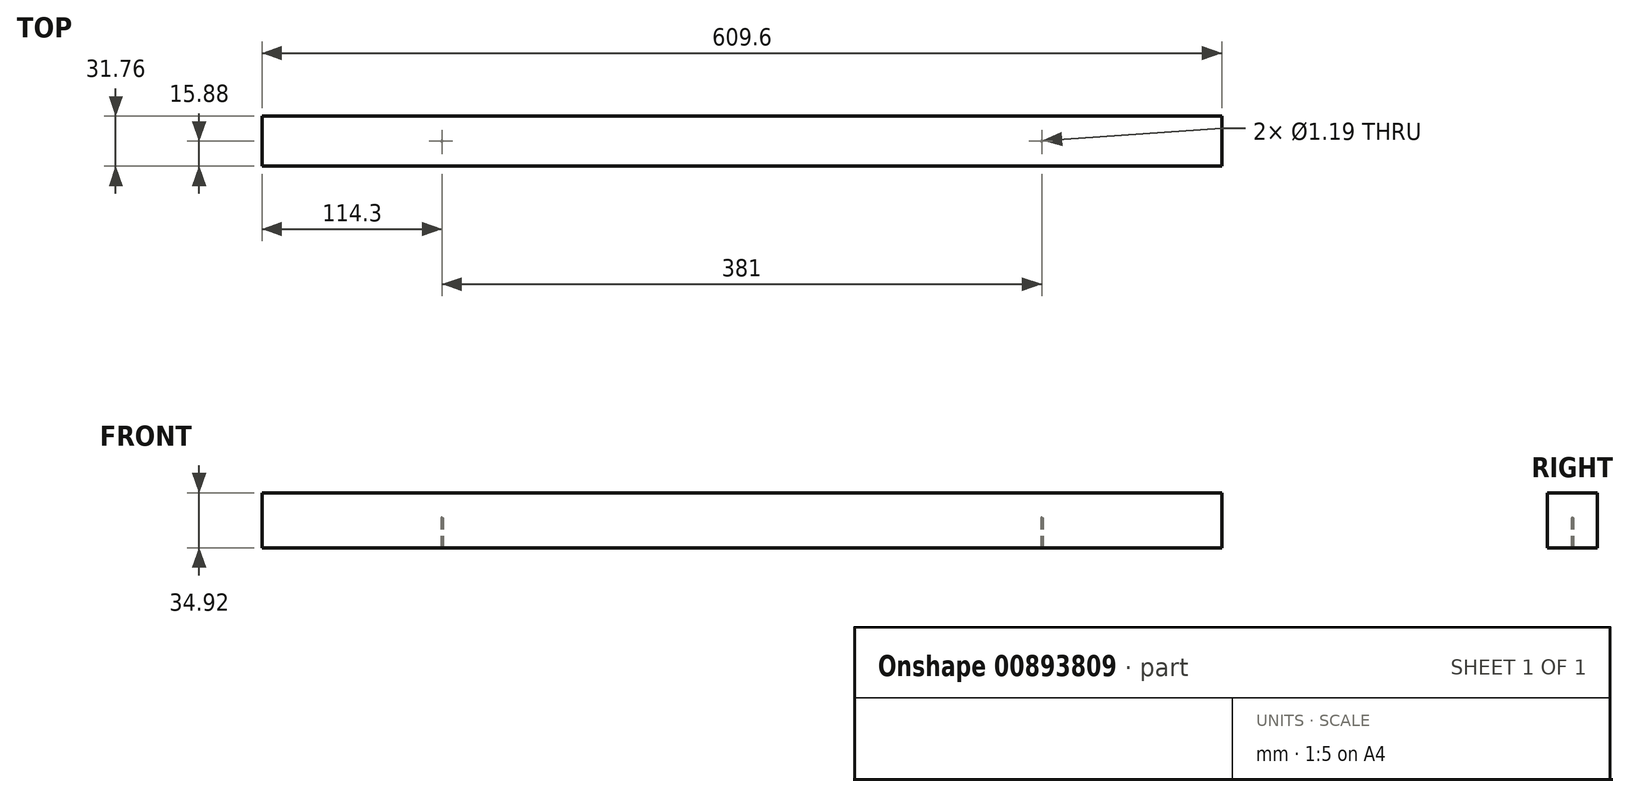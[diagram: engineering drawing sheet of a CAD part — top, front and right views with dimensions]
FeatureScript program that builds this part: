
annotation { "Feature Type Name" : "Feature", "Feature Type Description" : "" }
export const myFeature = defineFeature(function(context is Context, id is Id, definition is map)
    precondition{}
    {
        {
            var Q0;
            Q0=qCreatedBy(makeId("Top.planeOp"),FACE);
            var sketch = newSketch(context, id + "F0", { "sketchPlane" : qUnion([Q0])});
            skLineSegment(sketch, "E0.bottom", {"start": v(-304.8, 15.87) * mm, "end": v(304.8, 15.87) * mm});
            skLineSegment(sketch, "E0.top", {"start": v(-304.8, -15.87) * mm, "end": v(304.8, -15.87) * mm});
            skLineSegment(sketch, "E0.left", {"start": v(-304.8, 15.87) * mm, "end": v(-304.8, -15.87) * mm});
            skLineSegment(sketch, "E0.right", {"start": v(304.8, 15.87) * mm, "end": v(304.8, -15.87) * mm});
            skPoint(sketch, "E0.middle", {"position": v(0, 0) * mm});
            skSolve(sketch);
        }
        {
            var Q0;
            Q0=makeQuery(id+"F0.imprint","IMPRINT",FACE,{"disambiguationData":[TD([[makeQuery(id+"F0.imprint","IMPRINT",EDGE,{"derivedFrom":sQuery(id+"F0.wireOp",EDGE,"E0.bottom")}),-1.0]])]});
            extrude(context, id + "F1", {"entities" : qUnion([Q0]), "depth" : 34.92 * mm, "offsetDistance" : 25.4 * mm});
        }
        {
            var Q0;
            Q0=makeQuery(id+"F1.opExtrude","CAP_FACE",FACE,{"disambiguationData":[OSD([sQuery(id+"F0.wireOp",EDGE,"E0.bottom"),sQuery(id+"F0.wireOp",EDGE,"E0.top"),sQuery(id+"F0.wireOp",EDGE,"E0.left"),sQuery(id+"F0.wireOp",EDGE,"E0.right")])],"isStart":true});
            var sketch = newSketch(context, id + "F2", { "sketchPlane" : qUnion([Q0])});
            skPoint(sketch, "E1", {"position": v(-190.5, 0) * mm});
            skPoint(sketch, "E2", {"position": v(190.5, 0) * mm});
            skSolve(sketch);
        }
        {
            var Q0;
            Q0=sQuery(id+"F2.wireOp",VERTEX,"E1");
            var Q1;
            Q1=sQuery(id+"F2.wireOp",VERTEX,"E2");
            var Q2;
            Q2=makeQuery(id+"F1.opExtrude","SWEPT_BODY",BODY,{"disambiguationData":[OSD([sQuery(id+"F0.wireOp",EDGE,"E0.bottom"),sQuery(id+"F0.wireOp",EDGE,"E0.top"),sQuery(id+"F0.wireOp",EDGE,"E0.left"),sQuery(id+"F0.wireOp",EDGE,"E0.right")])]});
            hole(context, id + "F3", {"style" : HoleStyle.SIMPLE, "endStyle" : HoleEndStyle.BLIND, "holeDiameter" : 1.2 * mm, "majorDiameter" : 6.35 * mm, "holeDepth" : 19.05 * mm, "isTappedThrough" : true, "tappedDepth" : 12.7 * mm, "tapClearance" : 3, "startFromSketch" : true, "locations" : qUnion([Q0, Q1]), "scope" : qUnion([Q2])});
        }
    });
